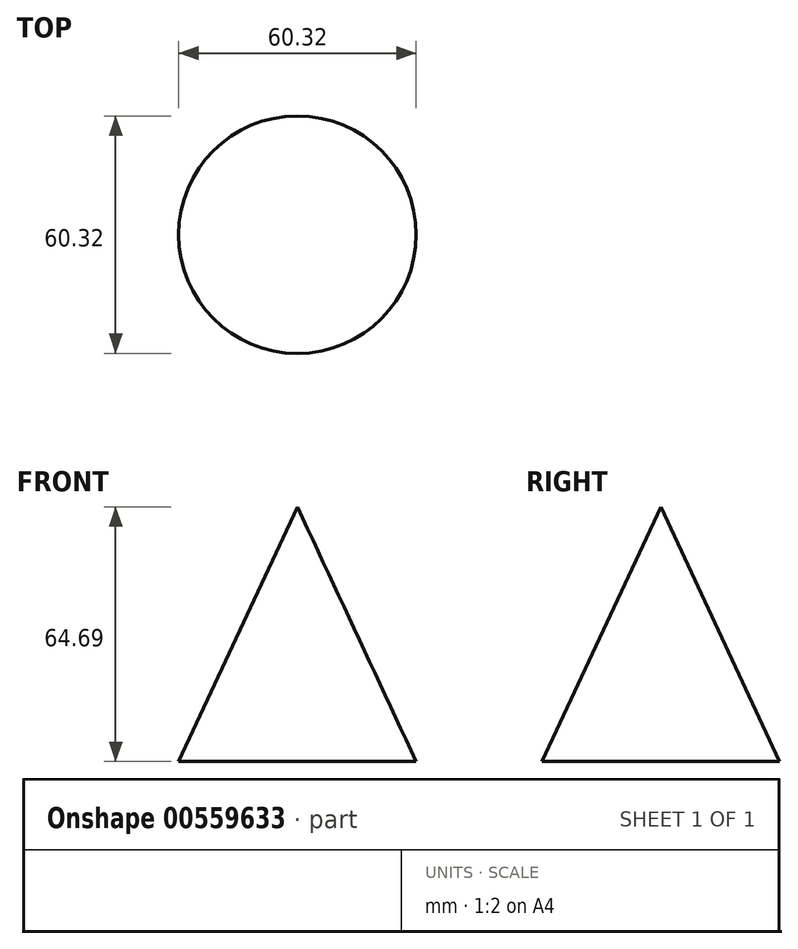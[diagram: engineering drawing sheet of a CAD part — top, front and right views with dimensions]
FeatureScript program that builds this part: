
annotation { "Feature Type Name" : "Feature", "Feature Type Description" : "" }
export const myFeature = defineFeature(function(context is Context, id is Id, definition is map)
    precondition{}
    {
        {
            var Q0;
            Q0=qCreatedBy(makeId("Top.planeOp"),FACE);
            var sketch = newSketch(context, id + "F0", { "sketchPlane" : qUnion([Q0])});
            skCircle(sketch, "E0", {"center": v(0, 0) * mm, "radius": 30.16 * mm});
            skSolve(sketch);
        }
        {
            var Q0;
            Q0=makeQuery(id+"F0.imprint","IMPRINT",FACE,{"disambiguationData":[TD([[makeQuery(id+"F0.imprint","IMPRINT",EDGE,{"derivedFrom":sQuery(id+"F0.wireOp",EDGE,"E0")}),1.0]])]});
            extrude(context, id + "F1", {"entities" : qUnion([Q0]), "depth" : 76.2 * mm, "offsetDistance" : 25.4 * mm, "hasDraft" : true, "draftAngle" : 25 * degree, "draftPullDirection" : true});
        }
    });
